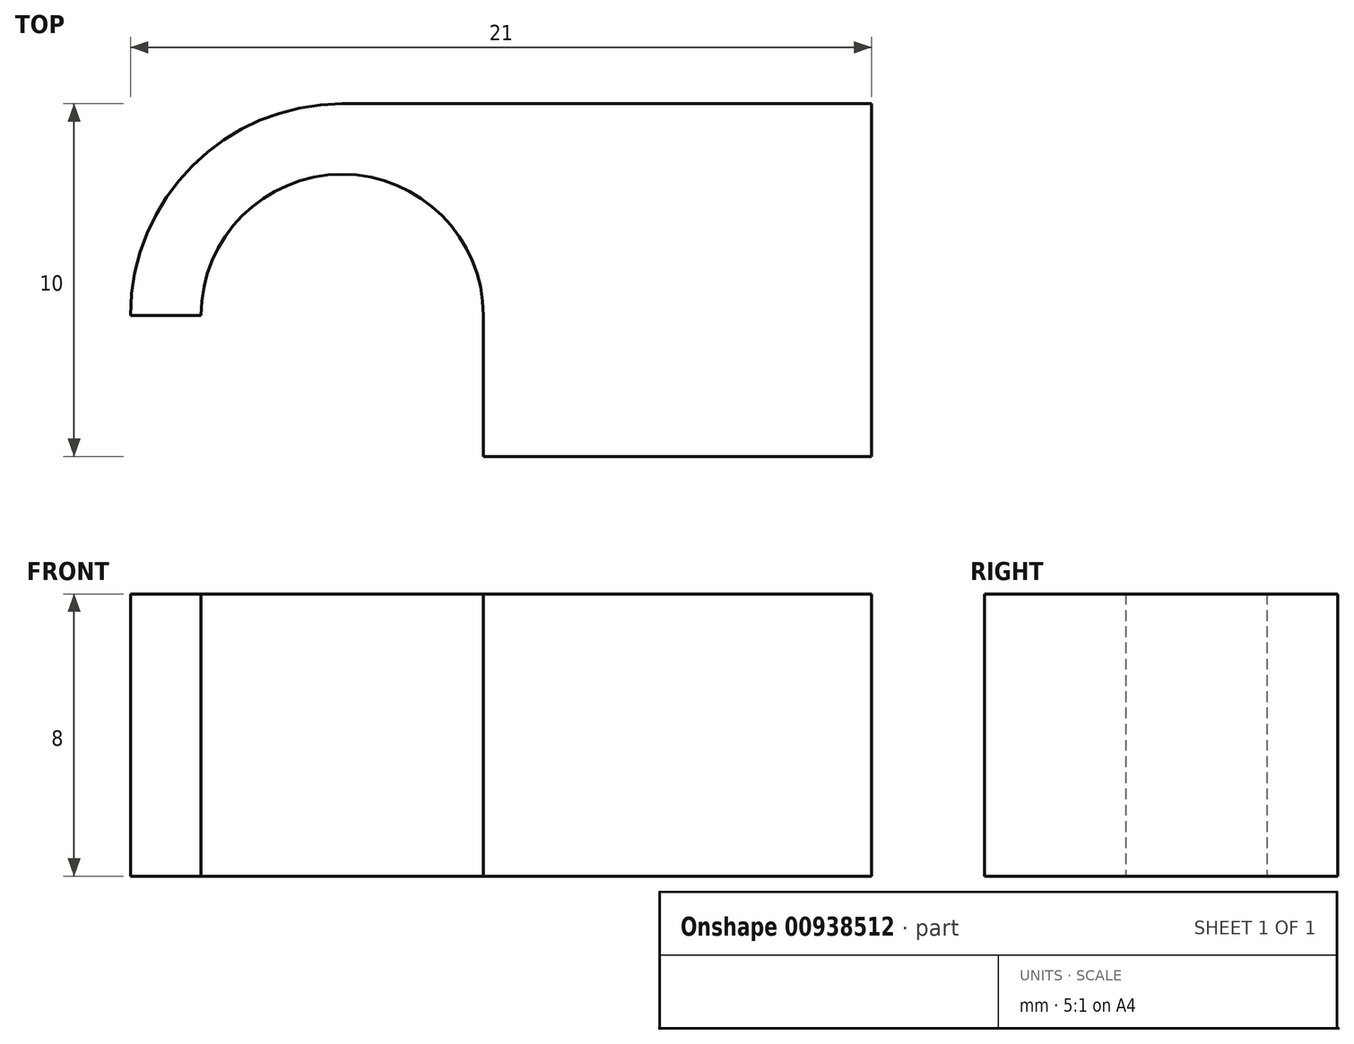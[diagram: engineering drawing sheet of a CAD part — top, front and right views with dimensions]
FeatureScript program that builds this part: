
annotation { "Feature Type Name" : "Feature", "Feature Type Description" : "" }
export const myFeature = defineFeature(function(context is Context, id is Id, definition is map)
    precondition{}
    {
        {
            var Q0;
            Q0=qCreatedBy(makeId("Top.planeOp"),FACE);
            var sketch = newSketch(context, id + "F0", { "sketchPlane" : qUnion([Q0])});
            skArc(sketch, "E0", {"start": v(4, 0) * mm, "mid": v(0, 4) * mm, "end": v(-4, 0) * mm});
            skArc(sketch, "E1.0", {"start": v(0, 6) * mm, "mid": v(-4.24, 4.24) * mm, "end": v(-6, 0) * mm});
            skLineSegment(sketch, "E2", {"start": v(0, 6) * mm, "end": v(15, 6) * mm});
            skLineSegment(sketch, "E3", {"start": v(4, -4) * mm, "end": v(15, -4) * mm});
            skLineSegment(sketch, "E4", {"start": v(15, 6) * mm, "end": v(15, -4) * mm});
            skLineSegment(sketch, "E5", {"start": v(-4, 0) * mm, "end": v(-6, 0) * mm});
            skLineSegment(sketch, "E6", {"start": v(4, 0) * mm, "end": v(4, -4) * mm});
            skPoint(sketch, "E7.orphan", {"position": v(0, -4) * mm});
            skSolve(sketch);
        }
        {
            var Q0;
            Q0=makeQuery(id+"F0.imprint","IMPRINT",FACE,{"disambiguationData":[TD([[makeQuery(id+"F0.imprint","IMPRINT",EDGE,{"derivedFrom":sQuery(id+"F0.wireOp",EDGE,"E0")}),-1.0]])]});
            extrude(context, id + "F1", {"entities" : qUnion([Q0]), "endBound" : BoundingType.SYMMETRIC, "depth" : 8 * mm, "offsetDistance" : 25 * mm});
        }
    });
